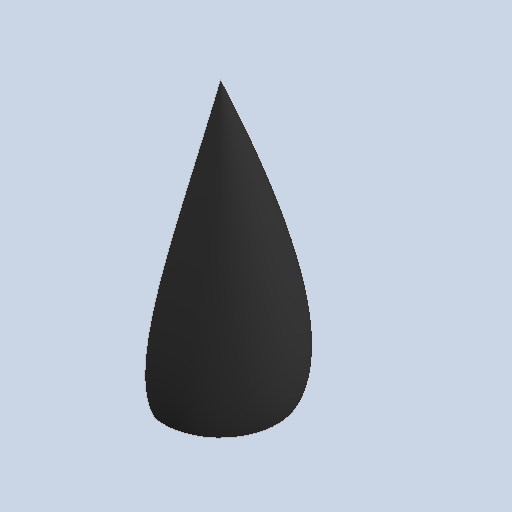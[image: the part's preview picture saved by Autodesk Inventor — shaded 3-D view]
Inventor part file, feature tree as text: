
AUTODESK INVENTOR PART (.ipt)
format: ipt  version: 2023 (Build 270158000, 158)  size: 342,528 bytes
history: native  units: mm
features: sketch x5, extrude x3, other x1, revolve x1, hole x1, fillet x1
ambient origin geometry x8: Origin, YZ Plane, XZ Plane, XY Plane, X Axis, Y Axis, Z Axis, Center Point
bodies: Body1 (feature_tree)
feature tree (12):
  other  "ソリッド1"
  revolve  "回転1"
  extrude  "押し出し3"  Depth=40.0mm
  hole  "穴1"  [1 undecoded]
  extrude  "押し出し4"  Depth=45.0mm
  extrude  "押し出し5"  Depth=40.0mm
  fillet  "フィレット2"  [1 undecoded]
  sketch  "スケッチ1"
  sketch  "スケッチ4"
  sketch  "スケッチ5"
  sketch  "スケッチ6"
  sketch  "スケッチ7"
note: 2 required parameter values undecoded (feature->parameter linkage not recoverable at this tier; creation-order binding heuristic only, values carry confidence <= 0.55)
